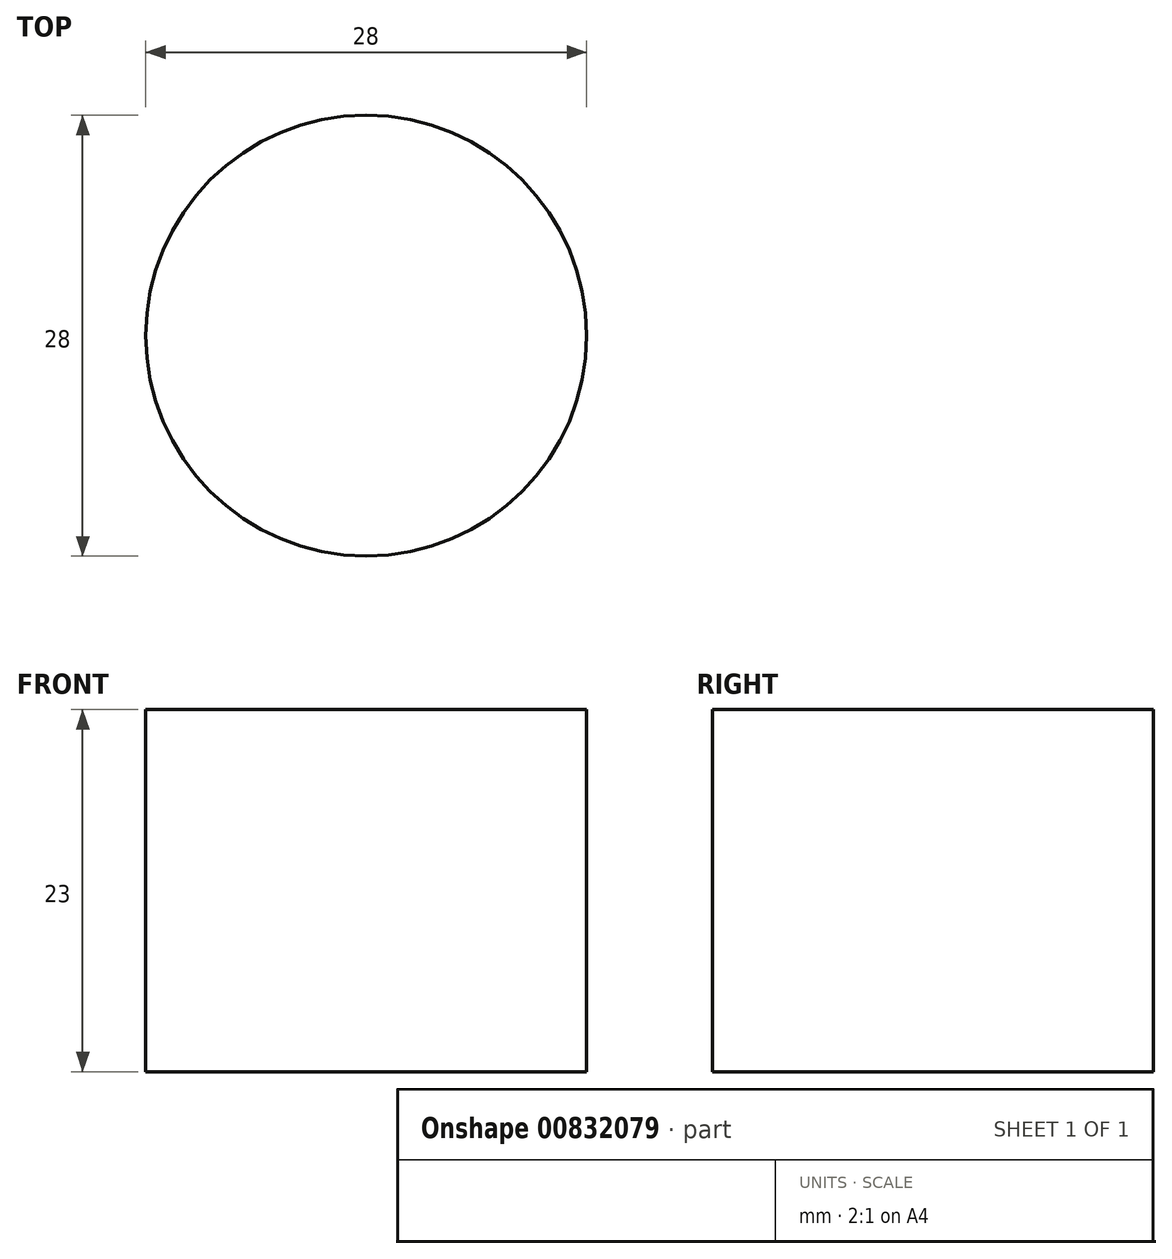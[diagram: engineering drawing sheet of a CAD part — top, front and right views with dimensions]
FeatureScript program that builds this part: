
annotation { "Feature Type Name" : "Feature", "Feature Type Description" : "" }
export const myFeature = defineFeature(function(context is Context, id is Id, definition is map)
    precondition{}
    {
        {
            var Q0;
            Q0=qCreatedBy(makeId("Top.planeOp"),FACE);
            var sketch = newSketch(context, id + "F0", { "sketchPlane" : qUnion([Q0])});
            skCircle(sketch, "E0", {"center": v(0, 0) * mm, "radius": 14 * mm});
            skSolve(sketch);
        }
        {
            var Q0;
            Q0 = qSketchRegion(id + "F0", true);
            extrude(context, id + "F1", {"entities" : qUnion([Q0]), "endBound" : BoundingType.SYMMETRIC, "depth" : 23 * mm, "offsetDistance" : 25 * mm});
        }
    });
